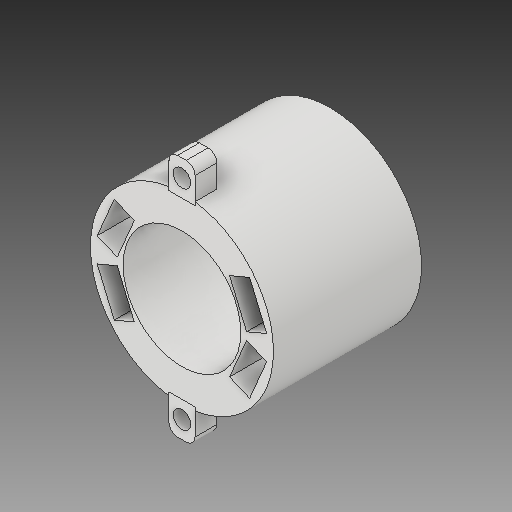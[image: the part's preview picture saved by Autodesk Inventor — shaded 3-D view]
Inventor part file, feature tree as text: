
AUTODESK INVENTOR PART (.ipt)
format: ipt  version: 2018.2 (Build 222227000, 227)  size: 180,224 bytes
history: native  units: in
note: dims shown in document units (in); Inventor stores cm internally (conversion verified against a paired STEP export)
features: fillet x1
ambient origin geometry x8: Origin, YZ Plane, XZ Plane, XY Plane, X Axis, Y Axis, Z Axis, Center Point
bodies: Solid1 (feature_tree)
feature tree (1):
  fillet  "Fillet2"  [1 undecoded]
note: 1 required parameter value undecoded (feature->parameter linkage not recoverable at this tier; creation-order binding heuristic only, values carry confidence <= 0.55)
